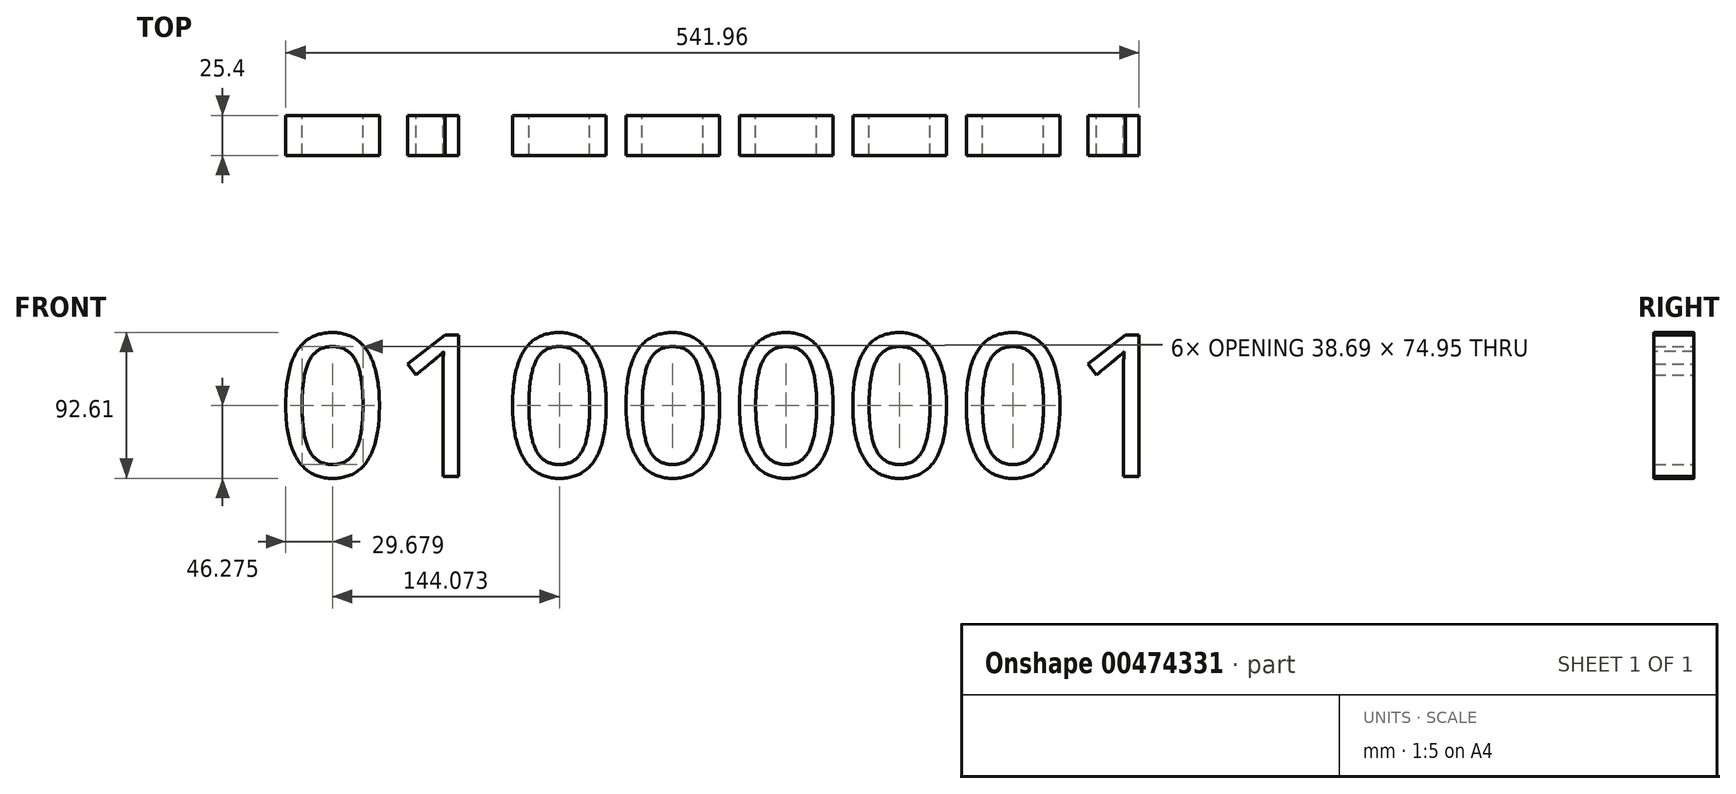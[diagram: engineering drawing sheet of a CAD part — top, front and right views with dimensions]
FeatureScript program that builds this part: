
annotation { "Feature Type Name" : "Feature", "Feature Type Description" : "" }
export const myFeature = defineFeature(function(context is Context, id is Id, definition is map)
    precondition{}
    {
        {
            var Q0;
            Q0=qCreatedBy(makeId("Front.planeOp"),FACE);
            var sketch = newSketch(context, id + "F0", { "sketchPlane" : qUnion([Q0])});
            skText(sketch, "E0", { "text": "01000001", "fontName": "OpenSans-Regular.ttf"});
            const initialGuessF0  = {"E0": [-0.04591, -0.06414, 1, 0, 0.09072]};
            skSetInitialGuess(sketch, initialGuessF0);
            skSolve(sketch);
        }
        {
            var Q0;
            Q0=qSketchRegion(id+"F0",true);
            extrude(context, id + "F1", {"entities" : qUnion([Q0]), "depth" : 25.4 * mm});
        }
    });
